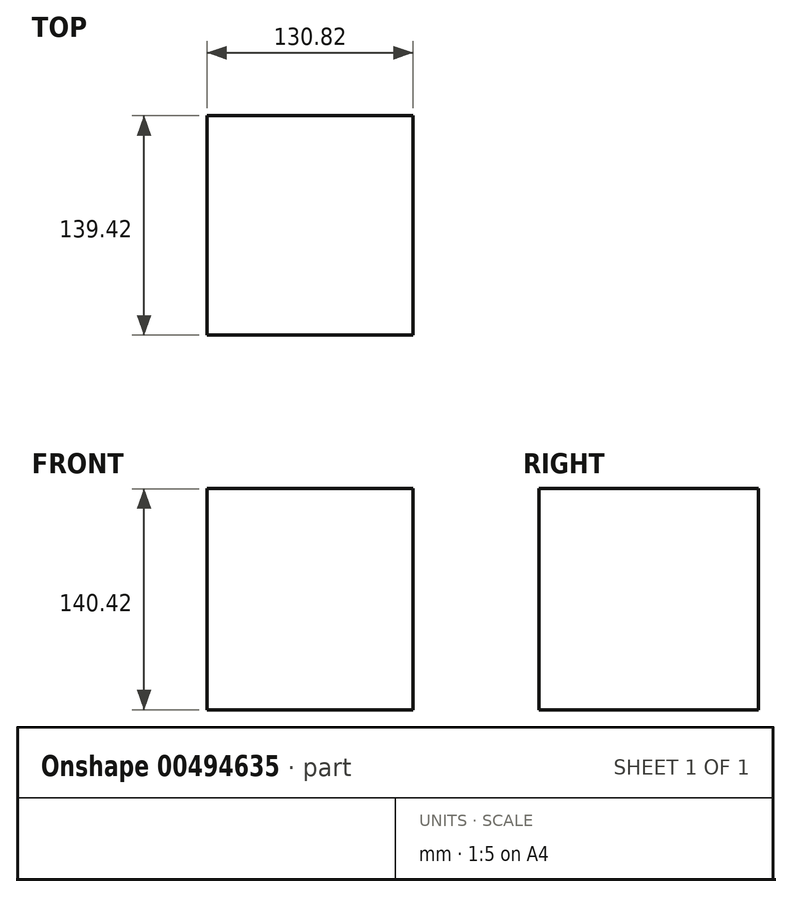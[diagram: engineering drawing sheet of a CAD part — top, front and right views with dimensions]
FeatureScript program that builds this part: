
annotation { "Feature Type Name" : "Feature", "Feature Type Description" : "" }
export const myFeature = defineFeature(function(context is Context, id is Id, definition is map)
    precondition{}
    {
        {
            var Q0;
            Q0=qCreatedBy(makeId("Front.planeOp"),FACE);
            var sketch = newSketch(context, id + "F0", { "sketchPlane" : qUnion([Q0])});
            skLineSegment(sketch, "E0.bottom", {"start": v(65.41, 70.21) * mm, "end": v(-65.41, 70.21) * mm});
            skLineSegment(sketch, "E0.top", {"start": v(65.41, -70.21) * mm, "end": v(-65.41, -70.21) * mm});
            skLineSegment(sketch, "E0.left", {"start": v(65.41, 70.21) * mm, "end": v(65.41, -70.21) * mm});
            skLineSegment(sketch, "E0.right", {"start": v(-65.41, 70.21) * mm, "end": v(-65.41, -70.21) * mm});
            skPoint(sketch, "E0.middle", {"position": v(0, 0) * mm});
            skSolve(sketch);
        }
        {
            var Q0;
            Q0=makeQuery(id+"F0.imprint","IMPRINT",FACE,{"disambiguationData":[TD([[makeQuery(id+"F0.imprint","IMPRINT",EDGE,{"derivedFrom":sQuery(id+"F0.wireOp",EDGE,"E0.bottom")}),1.0]])]});
            var sketch = newSketch(context, id + "F1", { "sketchPlane" : qUnion([Q0])});
            skSolve(sketch);
        }
        {
            var Q0;
            Q0=makeQuery(id+"F1.imprint","IMPRINT",FACE,{"disambiguationData":[TD([[makeQuery(id+"F1.imprint","IMPRINT",EDGE,{"derivedFrom":makeQuery(id+"F0.imprint","IMPRINT",EDGE,{"derivedFrom":sQuery(id+"F0.wireOp",EDGE,"E0.bottom")})}),1.0]])]});
            extrude(context, id + "F2", {"entities" : qUnion([Q0]), "depth" : 139.42 * mm});
        }
    });
